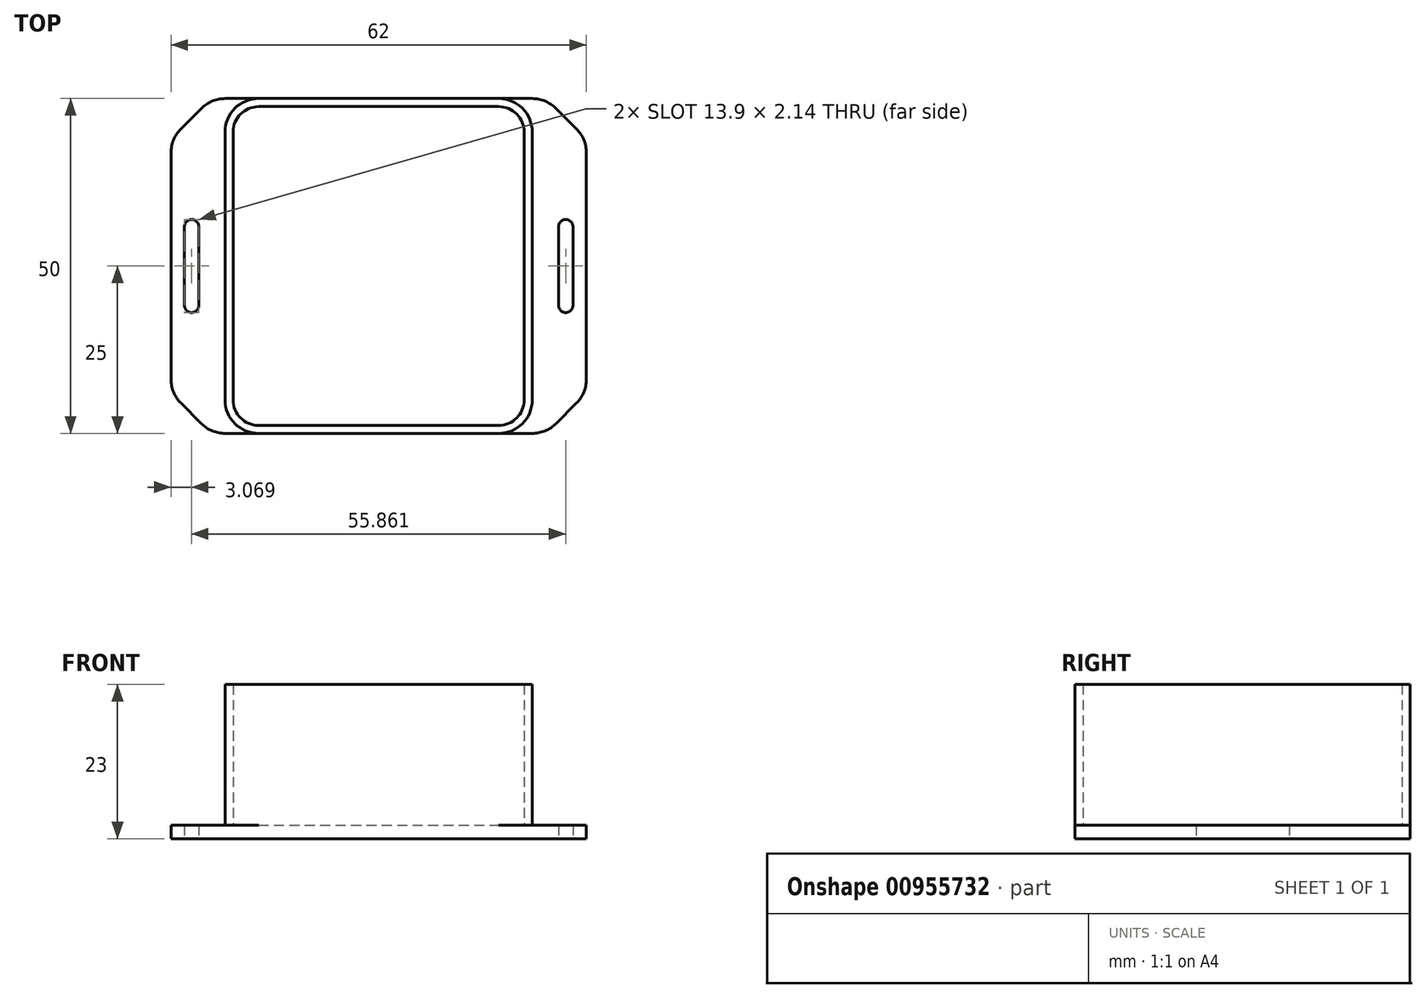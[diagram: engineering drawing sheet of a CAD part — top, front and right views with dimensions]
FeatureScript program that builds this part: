
annotation { "Feature Type Name" : "Feature", "Feature Type Description" : "" }
export const myFeature = defineFeature(function(context is Context, id is Id, definition is map)
    precondition{}
    {
        {
            var Q0;
            Q0=qCreatedBy(makeId("Top.planeOp"),FACE);
            var sketch = newSketch(context, id + "F0", { "sketchPlane" : qUnion([Q0])});
            skLineSegment(sketch, "E0", {"start": v(-57.46, 1.46) * mm, "end": v(-60.54, 4.54) * mm});
            skLineSegment(sketch, "E1", {"start": v(-62, 8.07) * mm, "end": v(-62, 41.93) * mm});
            skLineSegment(sketch, "E2", {"start": v(-60.54, 45.46) * mm, "end": v(-57.46, 48.54) * mm});
            skLineSegment(sketch, "E3", {"start": v(-53.93, 50) * mm, "end": v(-8.07, 50) * mm});
            skLineSegment(sketch, "E4", {"start": v(-4.54, 48.54) * mm, "end": v(-1.46, 45.46) * mm});
            skLineSegment(sketch, "E5", {"start": v(0, 41.93) * mm, "end": v(0, 8.07) * mm});
            skLineSegment(sketch, "E6", {"start": v(-1.46, 4.54) * mm, "end": v(-4.54, 1.46) * mm});
            skLineSegment(sketch, "E7", {"start": v(-8.07, 0) * mm, "end": v(-53.93, 0) * mm});
            skLineSegment(sketch, "E8", {"start": v(-4.14, 30.88) * mm, "end": v(-4.14, 19.12) * mm});
            skLineSegment(sketch, "E9", {"start": v(-2, 19.12) * mm, "end": v(-2, 30.88) * mm});
            skArc(sketch, "E10", {"start": v(-2, 30.88) * mm, "mid": v(-3.07, 31.95) * mm, "end": v(-4.14, 30.88) * mm});
            skArc(sketch, "E11", {"start": v(-4.14, 19.12) * mm, "mid": v(-3.07, 18.05) * mm, "end": v(-2, 19.12) * mm});
            skLineSegment(sketch, "E12", {"start": v(-31, 50) * mm, "end": v(-31, 0) * mm, "construction": true});
            skArc(sketch, "E13.MirrorCS", {"start": v(-60, 30.88) * mm, "mid": v(-58.93, 31.95) * mm, "end": v(-57.86, 30.88) * mm});
            skLineSegment(sketch, "E14.MirrorCS", {"start": v(-60, 19.12) * mm, "end": v(-60, 30.88) * mm});
            skLineSegment(sketch, "E15.MirrorCS", {"start": v(-57.86, 30.88) * mm, "end": v(-57.86, 19.12) * mm});
            skArc(sketch, "E16.MirrorCS", {"start": v(-57.86, 19.12) * mm, "mid": v(-58.93, 18.05) * mm, "end": v(-60, 19.12) * mm});
            skPoint(sketch, "E17.visualSharp", {"position": v(-56, 0) * mm});
            skArc(sketch, "E17.filletArc", {"start": v(-57.46, 1.46) * mm, "mid": v(-55.84, 0.38) * mm, "end": v(-53.93, 0) * mm});
            skPoint(sketch, "E18.visualSharp", {"position": v(-62, 6) * mm});
            skArc(sketch, "E18.filletArc", {"start": v(-62, 8.07) * mm, "mid": v(-61.62, 6.16) * mm, "end": v(-60.54, 4.54) * mm});
            skPoint(sketch, "E19.visualSharp", {"position": v(-62, 44) * mm});
            skArc(sketch, "E19.filletArc", {"start": v(-60.54, 45.46) * mm, "mid": v(-61.62, 43.84) * mm, "end": v(-62, 41.93) * mm});
            skPoint(sketch, "E20.visualSharp", {"position": v(-56, 50) * mm});
            skArc(sketch, "E20.filletArc", {"start": v(-53.93, 50) * mm, "mid": v(-55.84, 49.62) * mm, "end": v(-57.46, 48.54) * mm});
            skPoint(sketch, "E21.visualSharp", {"position": v(-6, 50) * mm});
            skArc(sketch, "E21.filletArc", {"start": v(-4.54, 48.54) * mm, "mid": v(-6.16, 49.62) * mm, "end": v(-8.07, 50) * mm});
            skPoint(sketch, "E22.visualSharp", {"position": v(0, 44) * mm});
            skArc(sketch, "E22.filletArc", {"start": v(0, 41.93) * mm, "mid": v(-0.38, 43.84) * mm, "end": v(-1.46, 45.46) * mm});
            skPoint(sketch, "E23.visualSharp", {"position": v(0, 6) * mm});
            skArc(sketch, "E23.filletArc", {"start": v(-1.46, 4.54) * mm, "mid": v(-0.38, 6.16) * mm, "end": v(0, 8.07) * mm});
            skPoint(sketch, "E24.visualSharp", {"position": v(-6, 0) * mm});
            skArc(sketch, "E24.filletArc", {"start": v(-8.07, 0) * mm, "mid": v(-6.16, 0.38) * mm, "end": v(-4.54, 1.46) * mm});
            skLineSegment(sketch, "E25", {"start": v(0, 25) * mm, "end": v(-62, 25) * mm, "construction": true});
            skLineSegment(sketch, "E26", {"start": v(-2, 25) * mm, "end": v(-4.14, 25) * mm, "construction": true});
            skSolve(sketch);
        }
        {
            var Q0;
            Q0=makeQuery(id+"F0.imprint","IMPRINT",FACE,{"disambiguationData":[TD([[makeQuery(id+"F0.imprint","IMPRINT",EDGE,{"derivedFrom":sQuery(id+"F0.wireOp",EDGE,"E0")}),-1.0]])]});
            extrude(context, id + "F1", {"entities" : qUnion([Q0]), "depth" : 2 * mm, "offsetDistance" : 25 * mm});
        }
        {
            var Q0;
            Q0=makeQuery(id+"F1.opExtrude","CAP_FACE",FACE,{"disambiguationData":[OSD([sQuery(id+"F0.wireOp",EDGE,"E0"),sQuery(id+"F0.wireOp",EDGE,"E1"),sQuery(id+"F0.wireOp",EDGE,"E2"),sQuery(id+"F0.wireOp",EDGE,"E3"),sQuery(id+"F0.wireOp",EDGE,"E4"),sQuery(id+"F0.wireOp",EDGE,"E5"),sQuery(id+"F0.wireOp",EDGE,"E6"),sQuery(id+"F0.wireOp",EDGE,"E7"),sQuery(id+"F0.wireOp",EDGE,"E8"),sQuery(id+"F0.wireOp",EDGE,"E9"),sQuery(id+"F0.wireOp",EDGE,"E10"),sQuery(id+"F0.wireOp",EDGE,"E11"),sQuery(id+"F0.wireOp",EDGE,"E13.MirrorCS"),sQuery(id+"F0.wireOp",EDGE,"E14.MirrorCS"),sQuery(id+"F0.wireOp",EDGE,"E15.MirrorCS"),sQuery(id+"F0.wireOp",EDGE,"E16.MirrorCS"),sQuery(id+"F0.wireOp",EDGE,"E17.filletArc"),sQuery(id+"F0.wireOp",EDGE,"E18.filletArc"),sQuery(id+"F0.wireOp",EDGE,"E19.filletArc"),sQuery(id+"F0.wireOp",EDGE,"E20.filletArc"),sQuery(id+"F0.wireOp",EDGE,"E21.filletArc"),sQuery(id+"F0.wireOp",EDGE,"E22.filletArc"),sQuery(id+"F0.wireOp",EDGE,"E23.filletArc"),sQuery(id+"F0.wireOp",EDGE,"E24.filletArc")])],"isStart":false});
            var sketch = newSketch(context, id + "F2", { "sketchPlane" : qUnion([Q0])});
            skLineSegment(sketch, "E27", {"start": v(-8.07, 5) * mm, "end": v(-8.07, 45) * mm});
            skLineSegment(sketch, "E28", {"start": v(-13.07, 50) * mm, "end": v(-48.93, 50) * mm});
            skLineSegment(sketch, "E29", {"start": v(-53.93, 45) * mm, "end": v(-53.93, 5) * mm});
            skLineSegment(sketch, "E30", {"start": v(-48.93, 0) * mm, "end": v(-13.07, 0) * mm});
            skPoint(sketch, "E31.visualSharp", {"position": v(-8.07, 0) * mm});
            skArc(sketch, "E31.filletArc", {"start": v(-13.07, 0) * mm, "mid": v(-9.54, 1.46) * mm, "end": v(-8.07, 5) * mm});
            skPoint(sketch, "E32.visualSharp", {"position": v(-53.93, 0) * mm});
            skArc(sketch, "E32.filletArc", {"start": v(-53.93, 5) * mm, "mid": v(-52.46, 1.46) * mm, "end": v(-48.93, 0) * mm});
            skPoint(sketch, "E33.visualSharp", {"position": v(-53.93, 50) * mm});
            skArc(sketch, "E33.filletArc", {"start": v(-48.93, 50) * mm, "mid": v(-52.46, 48.54) * mm, "end": v(-53.93, 45) * mm});
            skPoint(sketch, "E34.visualSharp", {"position": v(-8.07, 50) * mm});
            skArc(sketch, "E34.filletArc", {"start": v(-8.07, 45) * mm, "mid": v(-9.54, 48.54) * mm, "end": v(-13.07, 50) * mm});
            skLineSegment(sketch, "E35.0", {"start": v(-9.27, 5) * mm, "end": v(-9.27, 45) * mm});
            skArc(sketch, "E35.1", {"start": v(-13.07, 1.2) * mm, "mid": v(-10.38, 2.31) * mm, "end": v(-9.27, 5) * mm});
            skArc(sketch, "E35.2", {"start": v(-9.27, 45) * mm, "mid": v(-10.38, 47.69) * mm, "end": v(-13.07, 48.8) * mm});
            skLineSegment(sketch, "E35.3", {"start": v(-48.93, 1.2) * mm, "end": v(-13.07, 1.2) * mm});
            skLineSegment(sketch, "E35.4", {"start": v(-13.07, 48.8) * mm, "end": v(-48.93, 48.8) * mm});
            skArc(sketch, "E35.5", {"start": v(-48.93, 48.8) * mm, "mid": v(-51.62, 47.69) * mm, "end": v(-52.73, 45) * mm});
            skLineSegment(sketch, "E35.6", {"start": v(-52.73, 45) * mm, "end": v(-52.73, 5) * mm});
            skArc(sketch, "E35.7", {"start": v(-52.73, 5) * mm, "mid": v(-51.62, 2.31) * mm, "end": v(-48.93, 1.2) * mm});
            skSolve(sketch);
        }
        {
            var Q0;
            Q0=makeQuery(id+"F2.imprint","IMPRINT",FACE,{"disambiguationData":[TD([[makeQuery(id+"F2.imprint","IMPRINT",EDGE,{"derivedFrom":sQuery(id+"F2.wireOp",EDGE,"E27")}),1.0]])]});
            extrude(context, id + "F3", {"entities" : qUnion([Q0]), "operationType" : NewBodyOperationType.ADD, "depth" : 21 * mm, "offsetDistance" : 25 * mm});
        }
    });
